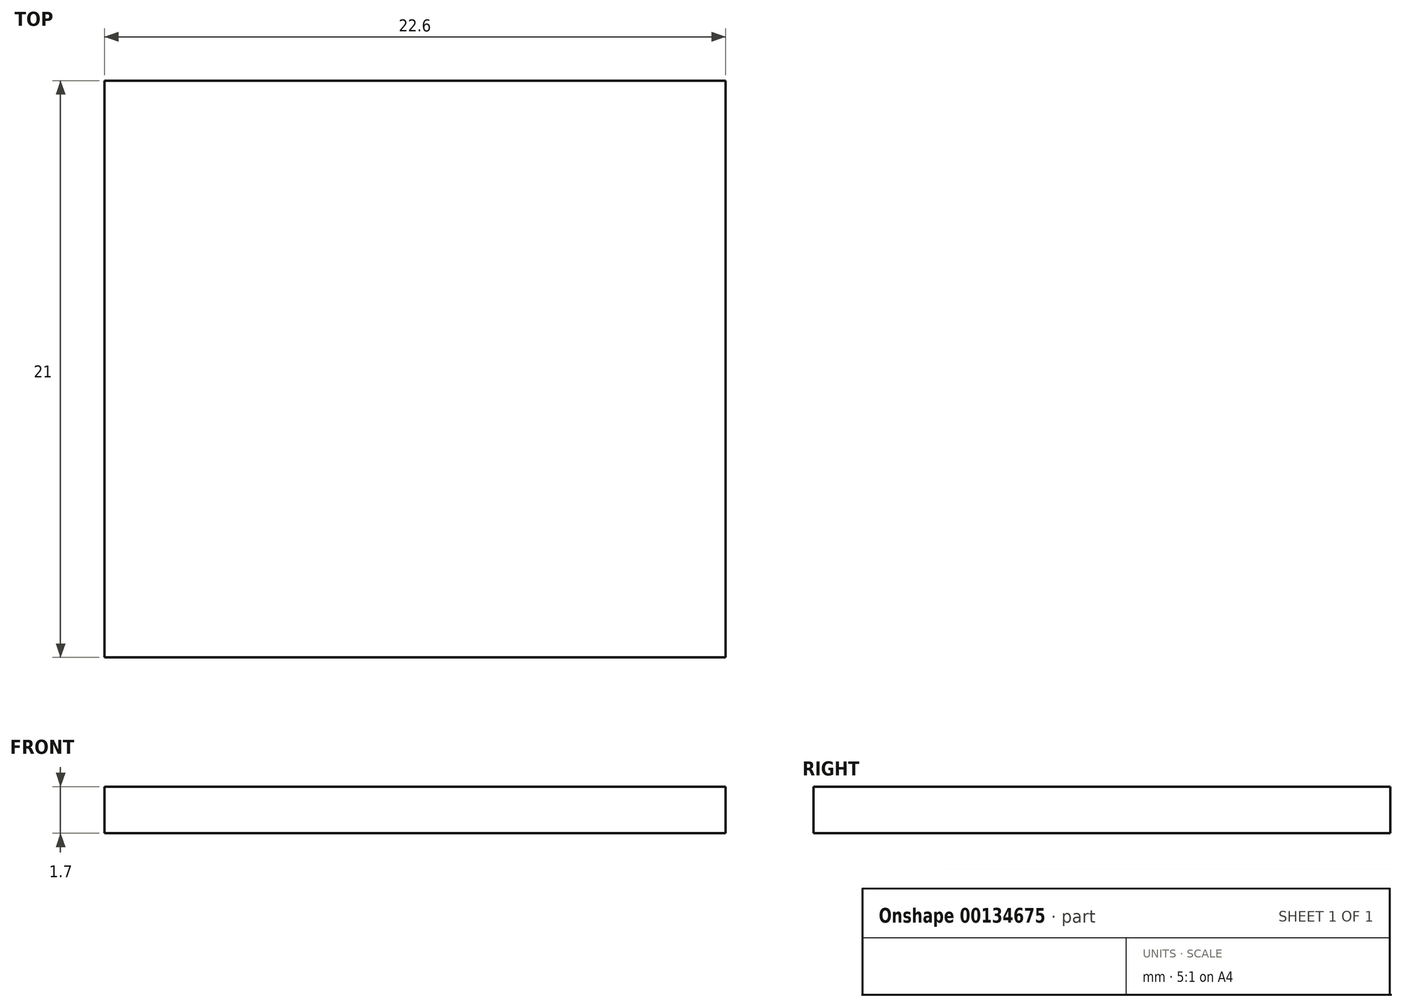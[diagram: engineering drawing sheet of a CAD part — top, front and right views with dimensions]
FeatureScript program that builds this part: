
annotation { "Feature Type Name" : "Feature", "Feature Type Description" : "" }
export const myFeature = defineFeature(function(context is Context, id is Id, definition is map)
    precondition{}
    {
        {
            assignVariable(context, id + "F0", {"name" : "pcb_height", "anyValue" : 1.7 * mm});
        }
        {
            var Q0;
            Q0=qCreatedBy(makeId("Top.planeOp"),FACE);
            var sketch = newSketch(context, id + "F1", { "sketchPlane" : qUnion([Q0])});
            skLineSegment(sketch, "E0.bottom", {"start": v(11.3, 10.5) * mm, "end": v(-11.3, 10.5) * mm});
            skLineSegment(sketch, "E0.top", {"start": v(11.3, -10.5) * mm, "end": v(-11.3, -10.5) * mm});
            skLineSegment(sketch, "E0.left", {"start": v(11.3, 10.5) * mm, "end": v(11.3, -10.5) * mm});
            skLineSegment(sketch, "E0.right", {"start": v(-11.3, 10.5) * mm, "end": v(-11.3, -10.5) * mm});
            skPoint(sketch, "E0.middle", {"position": v(0, 0) * mm});
            skSolve(sketch);
        }
        {
            var Q0;
            Q0=makeQuery(id+"F1.imprint","IMPRINT",FACE,{"disambiguationData":[TD([[makeQuery(id+"F1.imprint","IMPRINT",EDGE,{"derivedFrom":sQuery(id+"F1.wireOp",EDGE,"E0.bottom")}),1.0]])]});
            extrude(context, id + "F2", {"entities" : qUnion([Q0]), "depth" : getVariable(context, 'pcb_height')});
        }
    });
